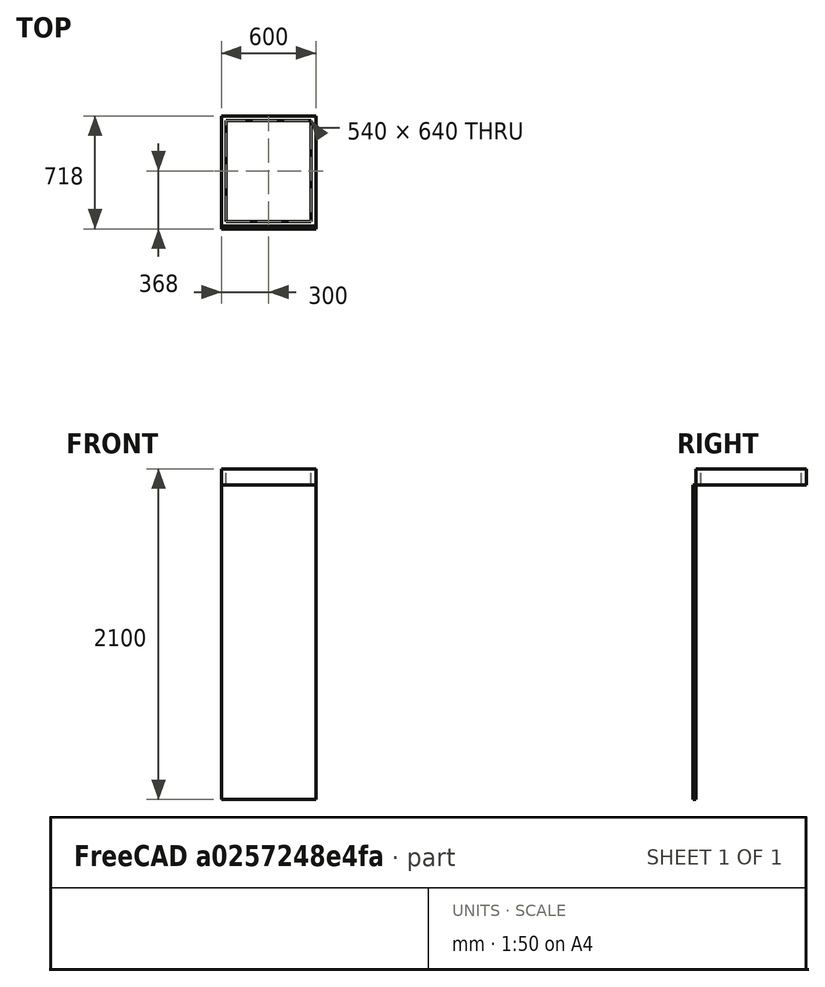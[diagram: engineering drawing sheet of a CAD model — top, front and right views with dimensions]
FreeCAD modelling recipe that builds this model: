
FCSTD DOCUMENT  (FreeCAD 0.22R37898 (Git))
Label: mesa
License: All rights reserved
objects: Sketcher::SketchObject×2, PartDesign::Pad×2, PartDesign::Body×2, App::Link×2, Assembly::JointGroup×1, Assembly::AssemblyObject×1
note: 8 computed .brp shape members not serialized (recipe doc carries the construction recipe); baked Part::Feature solids carry a one-line shape summary decoded from their .brp

FEATURE [Sketcher::SketchObject] Sketch
  AttachmentSupport = -> [XY_Plane]
  FullyConstrained = true
  MapMode = 5
  sketch-geometry (8):
    g0: LineSegment StartX=0 StartY=0 StartZ=0 EndX=600 EndY=0 EndZ=0
    g1: LineSegment StartX=600 StartY=0 StartZ=0 EndX=600 EndY=700 EndZ=0
    g2: LineSegment StartX=600 StartY=700 StartZ=0 EndX=0 EndY=700 EndZ=0
    g3: LineSegment StartX=0 StartY=700 StartZ=0 EndX=0 EndY=0 EndZ=0
    g4: LineSegment StartX=30 StartY=670 StartZ=0 EndX=30 EndY=30 EndZ=0
    g5: LineSegment StartX=30 StartY=30 StartZ=0 EndX=570 EndY=30 EndZ=0
    g6: LineSegment StartX=570 StartY=30 StartZ=0 EndX=570 EndY=670 EndZ=0
    g7: LineSegment StartX=570 StartY=670 StartZ=0 EndX=30 EndY=670 EndZ=0
  constraints (23):
    c: Coincident(g0,g1)
    c: Coincident(g1,g2)
    c: Coincident(g2,g3)
    c: Coincident(g3,g0)
    c: Horizontal(g0)
    c: Horizontal(g2)
    c: Vertical(g1)
    c: Vertical(g3)
    c: Distance(g1,g3) = 600
    c: Distance(g0,g2) = 700
    c: Coincident(g0,g-1)
    c: Coincident(g4,g5)
    c: Coincident(g5,g6)
    c: Coincident(g6,g7)
    c: Coincident(g7,g4)
    c: Vertical(g4)
    c: Vertical(g6)
    c: Horizontal(g5)
    c: Horizontal(g7)
    c: Distance(g4,g3) = 30
    c: Distance(g1,g6) = 30
    c: Distance(g7,g2) = 30
    c: Distance(g0,g5) = 30
FEATURE [PartDesign::Pad] Pad
  Direction = (0,0,1)
  Length = 100
  Length2 = 10
  Profile = -> Sketch
  ReferenceAxis = -> Sketch [N_Axis]
  Refine = true
  Suppressed = false
  Type = 0
FEATURE [PartDesign::Body] Body  label="patas mesa"
  AllowCompound = false
  Group = -> [Sketch,Pad]
  Origin = -> Origin
  Tip = -> Pad
FEATURE [Sketcher::SketchObject] Sketch001
  AttachmentSupport = -> [XZ_Plane001]
  FullyConstrained = true
  MapMode = 5
  Placement = pos=(0,0,0) rot=(1,0,0;1.5708rad)
  sketch-geometry (4):
    g0: LineSegment StartX=0 StartY=0 StartZ=0 EndX=0 EndY=-2000 EndZ=0
    g1: LineSegment StartX=0 StartY=-2000 StartZ=0 EndX=600 EndY=-2000 EndZ=0
    g2: LineSegment StartX=600 StartY=-2000 StartZ=0 EndX=600 EndY=0 EndZ=0
    g3: LineSegment StartX=600 StartY=0 StartZ=0 EndX=0 EndY=0 EndZ=0
  constraints (11):
    c: Coincident(g0,g1)
    c: Coincident(g1,g2)
    c: Coincident(g2,g3)
    c: Coincident(g3,g0)
    c: Vertical(g0)
    c: Vertical(g2)
    c: Horizontal(g1)
    c: Horizontal(g3)
    c: Distance(g0,g2) = 600
    c: Distance(g1,g3) = 2000
    c: Coincident(g0,g-1)
FEATURE [PartDesign::Pad] Pad001
  Direction = (0,-1,2e-16)
  Length = 18
  Length2 = 10
  Placement = pos=(0,0,0) rot=(1,0,0;1.5708rad)
  Profile = -> Sketch001
  ReferenceAxis = -> Sketch001 [N_Axis]
  Refine = true
  Suppressed = false
  Type = 0
FEATURE [PartDesign::Body] Body001  label="tabla mesa"
  AllowCompound = false
  Group = -> [Sketch001,Pad001]
  Origin = -> Origin001
  Tip = -> Pad001
FEATURE [Assembly::JointGroup] Joints
FEATURE [App::Link] patas_mesa  label="patas mesa001"
  LinkPlacement = pos=(-0.169098,-719.253,-100.004) rot=(0,0,1;0rad)
  LinkedObject = -> Body
  Placement = pos=(-0.169098,-719.253,-100.004) rot=(0,0,1;0rad)
FEATURE [App::Link] patas_mesa001  label="patas mesa002"
  LinkPlacement = pos=(-6.64372,-724.761,-1990.96) rot=(0,0,1;0rad)
  LinkedObject = -> Body
  Placement = pos=(-6.64372,-724.761,-1990.96) rot=(0,0,1;0rad)
FEATURE [Assembly::AssemblyObject] Assembly
  Group = -> [Joints,patas_mesa,patas_mesa001]
  Origin = -> Origin002
  Type = Assembly
